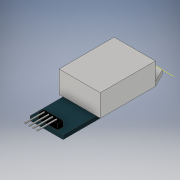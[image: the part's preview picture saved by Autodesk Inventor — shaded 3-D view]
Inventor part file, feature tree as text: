
AUTODESK INVENTOR PART (.ipt)
format: ipt  version: 2017.2 (Build 212223000, 223)  size: 186,880 bytes
history: native  units: in
note: dims shown in document units (in); Inventor stores cm internally (conversion verified against a paired STEP export)
features: sketch x7, extrude x5, projected_geometry x2, other x1, hole x1
ambient origin geometry x8: Origin, YZ Plane, XZ Plane, XY Plane, X Axis, Y Axis, Z Axis, Center Point
bodies: Solid1 (feature_tree)
feature tree (16):
  extrude  "Extrusion1"  Depth=0.4724in
  extrude  "Extrusion2"  Depth=0.7874in
  extrude  "Extrusion3"  Depth=0.0591in TaperAngle=0.0deg
  extrude  "Extrusion4"  Depth=0.7874in
  sketch  "Sketch5"  dims[d16=0.5906in d19=0.3937in]
  extrude  "Extrusion5"  Depth=0.3937in
  other  "Work Axis1"
  hole  "Hole1"  [1 undecoded]
  sketch  "Sketch1"  dims[d0=1.1024in d1=0.4724in]
  sketch  "Sketch2"  dims[d3=0.5906in d4=0.7874in]
  sketch  "Sketch3"  dims[d5=0.7874in d9=0.0591in d10=0.0in]
  sketch  "Sketch4"  dims[d14=0.5906in d15=0.7874in]
  sketch  "Sketch6"  dims[d20=0.0591in d21=0.0in d22=0.2559in d23=0.0in]
  sketch  "Sketch7"  dims[d27=0.2756in d28=0.0787in d29=0.2756in d30=0.0787in d31=0.0in d33=0.0197in d34=0.0197in d35=0.0197in d36=0.0197in d37=0.2362in d38=0.0394in d39=0.0in d40=0.0in d44=0.1181in d45=0.1181in d46=0.75in d47=0.119in d48=0.25in d49=0.5635in d50=1.0in d51=0.8108in]
  projected_geometry  "Projected Loop1"
  projected_geometry  "Project Cut Edges1"
note: 1 required parameter value undecoded (feature->parameter linkage not recoverable at this tier; creation-order binding heuristic only, values carry confidence <= 0.55)
